# Revit family: QF_Moffat_ICEM051E--
name_source: partatom
category: Specialty Equipment
units: mm (PartAtom-declared; Revit-internal decimal feet)

## family parameters
Always vertical = Yes
Cut with Voids When Loaded = No
OmniClass Number = 23.40.40.14.17.11
OmniClass Title = Cookers, Ovens, Stoves
Part Type = Normal
Room Calculation Point = No
Round Connector Dimension = Use Diameter
Shared = No
Work Plane-Based = No

## types (1)
- ICEM051E
    Apparent Power = 7250 VA
    Assembly Code = E1090320
    Cold Water Maximum Pressure = 50000.0 Pa
    Cold Water Minimum Pressure = 20000.0 Pa
    Cold Water Size = 1"
    Cold Water Temperature Recommended = 0 °C
    Cycle = 50 Hz
    Description = ELECTRIC DIRECT STEAM COMBI OVEN - 5 X 1/1 GN - 5 X 600 X 400 ● ELECTROMECHANICAL CONTROLS
    FL Amps = 11 A
    Filtered Water Supply Size = 1"
    HP = 9.722395000000
    Indirect Waste Flow = 0.0 L/s
    Indirect Waste Size = 1 1/2"
    Manufacturer = MOFFAT
    Max Overcurrent Protection = 0 A
    Min Ckt Ampacity = 0 A
    Model = ICEM051E
    Phase = 3
    URL = www.moffat.com
    URL Cutsheet = www.moffat.com
    Volts = 400 V
    Watts = 7250 W
    Weight in Pounds = 163

## geometry (parser evidence)
native form markers: Sweep x9
no freeform markers — native parametric forms only
